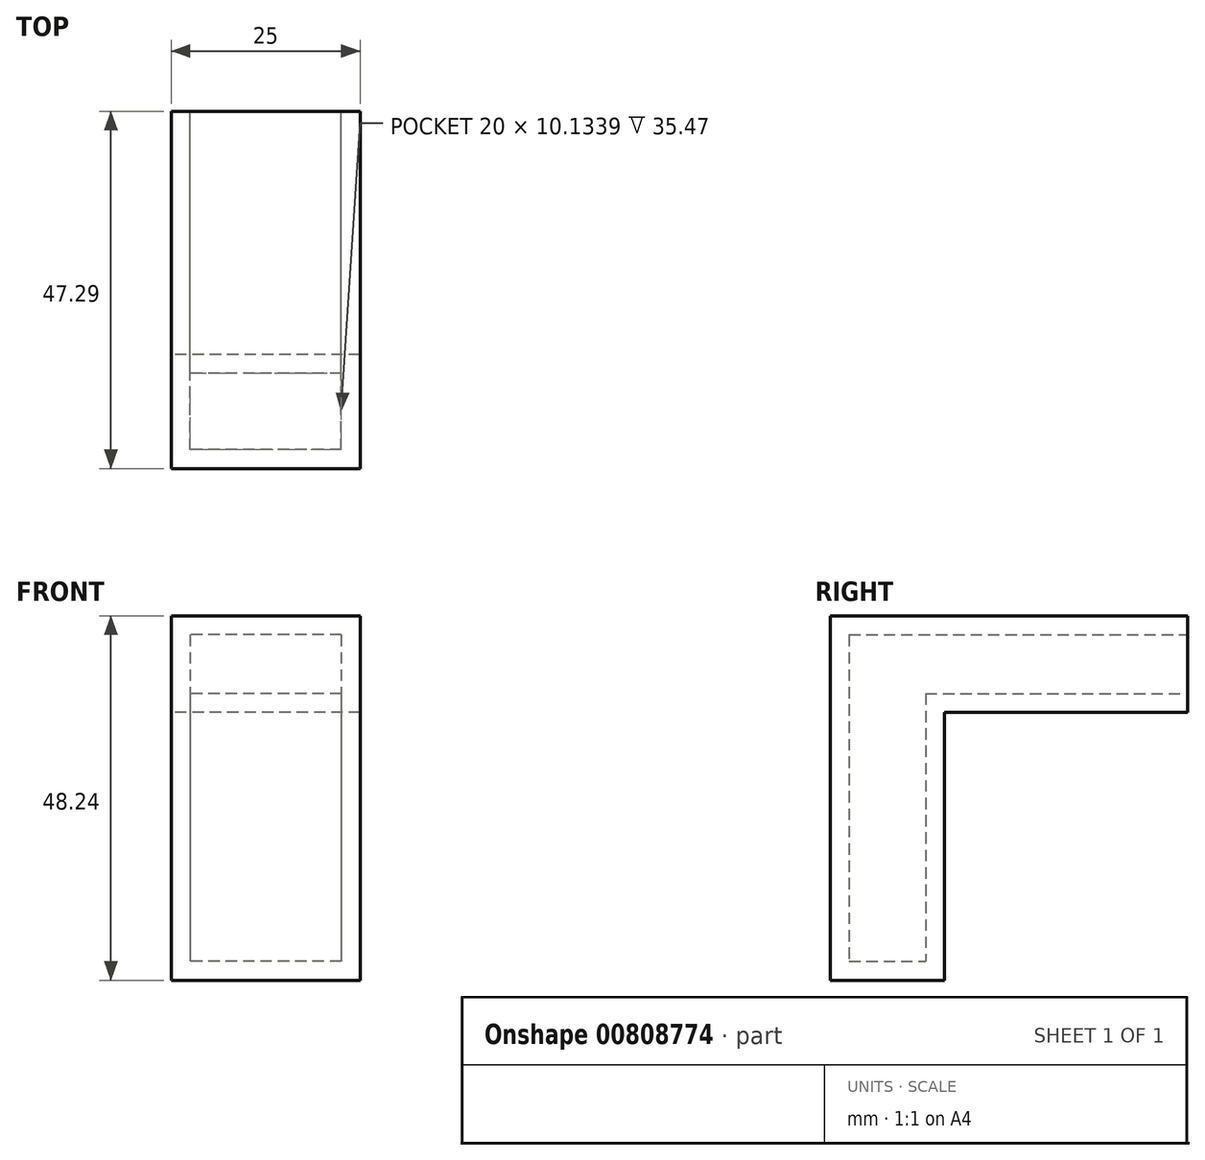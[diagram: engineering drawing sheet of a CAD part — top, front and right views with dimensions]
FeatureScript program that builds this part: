
annotation { "Feature Type Name" : "Feature", "Feature Type Description" : "" }
export const myFeature = defineFeature(function(context is Context, id is Id, definition is map)
    precondition{}
    {
        {
            var Q0;
            Q0=qCreatedBy(makeId("Right.planeOp"),FACE);
            var sketch = newSketch(context, id + "F0", { "sketchPlane" : qUnion([Q0])});
            skLineSegment(sketch, "E0.bottom", {"start": v(-33.52, 19.97) * mm, "end": v(-18.39, 19.97) * mm});
            skLineSegment(sketch, "E0.top", {"start": v(-33.52, -28.27) * mm, "end": v(-18.39, -28.27) * mm});
            skLineSegment(sketch, "E0.left", {"start": v(-33.52, 19.97) * mm, "end": v(-33.52, -28.27) * mm});
            skLineSegment(sketch, "E0.right", {"start": v(-18.39, 19.97) * mm, "end": v(-18.39, -28.27) * mm});
            skLineSegment(sketch, "E1.bottom", {"start": v(-18.39, 19.97) * mm, "end": v(13.77, 19.97) * mm});
            skLineSegment(sketch, "E1.top", {"start": v(-18.39, 7.2) * mm, "end": v(13.77, 7.2) * mm});
            skLineSegment(sketch, "E1.left", {"start": v(-18.39, 19.97) * mm, "end": v(-18.39, 7.2) * mm});
            skLineSegment(sketch, "E1.right", {"start": v(13.77, 19.97) * mm, "end": v(13.77, 7.2) * mm});
            skPoint(sketch, "E2.oppositeSnap0", {"position": v(-33.52, -4.15) * mm});
            skSolve(sketch);
        }
        {
            var Q0;
            Q0=makeQuery(id+"F0.imprint","IMPRINT",FACE,{"disambiguationData":[TD([[makeQuery(id+"F0.imprint","IMPRINT",EDGE,{"derivedFrom":sQuery(id+"F0.wireOp",EDGE,"E1.bottom")}),-1.0]])]});
            var Q1;
            Q1=makeQuery(id+"F0.imprint","IMPRINT",FACE,{"disambiguationData":[TD([[makeQuery(id+"F0.imprint","IMPRINT",EDGE,{"derivedFrom":sQuery(id+"F0.wireOp",EDGE,"E0.bottom")}),-1.0]])]});
            extrude(context, id + "F1", {"entities" : qUnion([Q0, Q1]), "depth" : 25 * mm, "offsetDistance" : 25 * mm});
        }
        {
            var Q0;
            Q0=makeQuery(id+"F1.opExtrude","SWEPT_FACE",FACE,{"disambiguationData":[OSD([sQuery(id+"F0.wireOp",EDGE,"E1.right")])]});
            shell(context, id + "F2", {"entities" : qUnion([Q0]), "thickness" : 2.5 * mm});
        }
    });
